# Revit family: Кровать палатная механическая
name_source: partatom
category: Оборудование
revit_build: Autodesk Revit 2017 (Build: 20170118_1100(x64)
units: mm (PartAtom-declared; Revit-internal decimal feet)

## family parameters
Всегда вертикально = Да
Заголовок OmniClass = General Furniture and Specialties
На основе рабочей плоскости = Нет
Номер OmniClass = 23.40.20.00
Общий = Нет
При загрузке вырезать с полостями = Нет
Размер круглого соединителя = Использовать диаметр
Тип детали = Нормальный
Точка расчета площади = Нет

## types (1)
- Eleganza 3 ХС
    Bed Caster Wheel = Caster-Wheel
    Bed Caster Wheel Frame = Metal - Painted White
    Bed Frame = Plastic - White
    Bed Frame Support = Ivory Porcelain,Glossy
    Bed Head Frame = Laminate - Ivory,Matte
    Bed Matress = Paint - White
    Bed Side Frame = Metal - Aluminum, Brushed
    Глубина ложа = 860 мм
    Общ_Высота = 775 мм
    Общ_Глубина = 1000 мм
    Общ_Единицы измерения = шт.
    Общ_Масса = 100
    Общ_Наименование = Кровать палатная
    Общ_Позиция = 20
    Общ_Поставщик = Linet
    Общ_Тип, марка = Praktika
    Общ_Ширина = 2200 мм
    Ширина ложа = 2080 мм

## geometry (parser evidence)
native form markers: Sweep x17
no freeform markers — native parametric forms only
